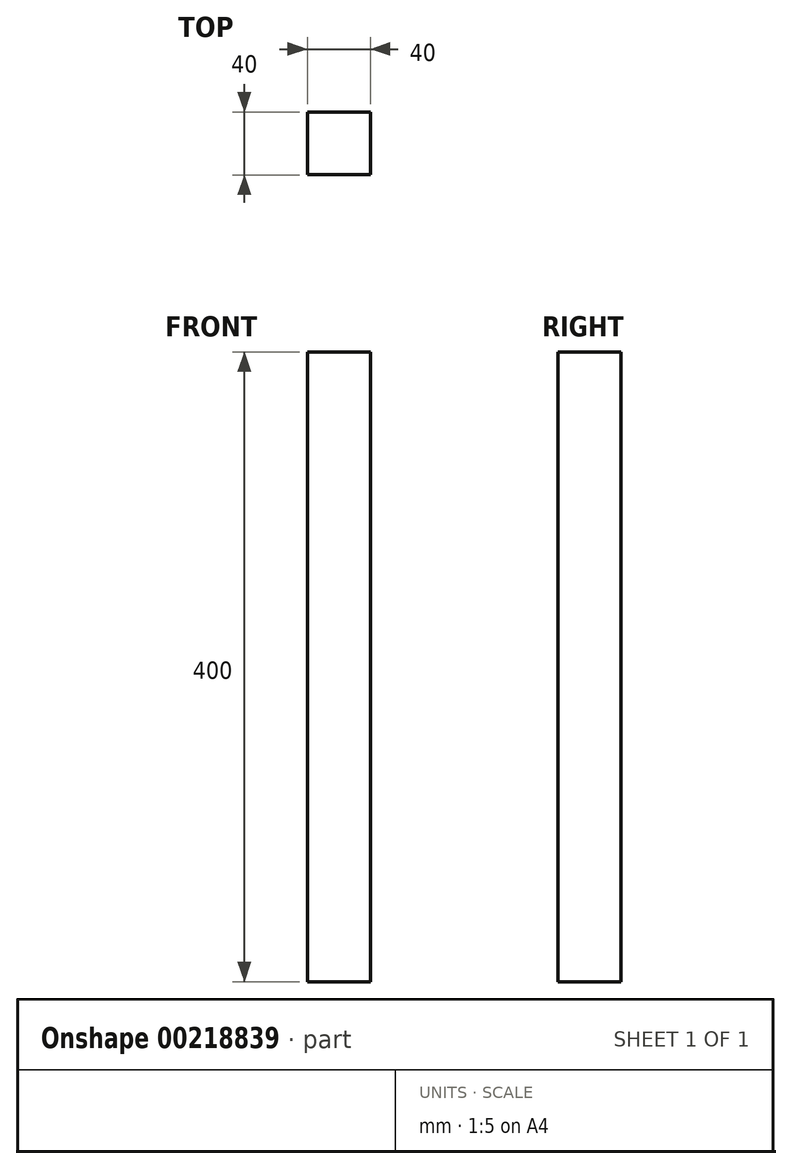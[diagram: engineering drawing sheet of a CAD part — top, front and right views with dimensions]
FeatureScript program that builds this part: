
annotation { "Feature Type Name" : "Feature", "Feature Type Description" : "" }
export const myFeature = defineFeature(function(context is Context, id is Id, definition is map)
    precondition{}
    {
        {
            var Q0;
            Q0=qCreatedBy(makeId("Top.planeOp"),FACE);
            var sketch = newSketch(context, id + "F0", { "sketchPlane" : qUnion([Q0])});
            skLineSegment(sketch, "E0.bottom", {"start": v(-61.03, 43.54) * mm, "end": v(-21.03, 43.54) * mm});
            skLineSegment(sketch, "E0.top", {"start": v(-61.03, 3.54) * mm, "end": v(-21.03, 3.54) * mm});
            skLineSegment(sketch, "E0.left", {"start": v(-61.03, 43.54) * mm, "end": v(-61.03, 3.54) * mm});
            skLineSegment(sketch, "E0.right", {"start": v(-21.03, 43.54) * mm, "end": v(-21.03, 3.54) * mm});
            skSolve(sketch);
        }
        {
            var Q0;
            Q0=makeQuery(id+"F0.imprint","IMPRINT",FACE,{"disambiguationData":[TD([[makeQuery(id+"F0.imprint","IMPRINT",EDGE,{"derivedFrom":sQuery(id+"F0.wireOp",EDGE,"E0.bottom")}),-1.0]])]});
            extrude(context, id + "F1", {"entities" : qUnion([Q0]), "depth" : 400 * mm});
        }
    });
